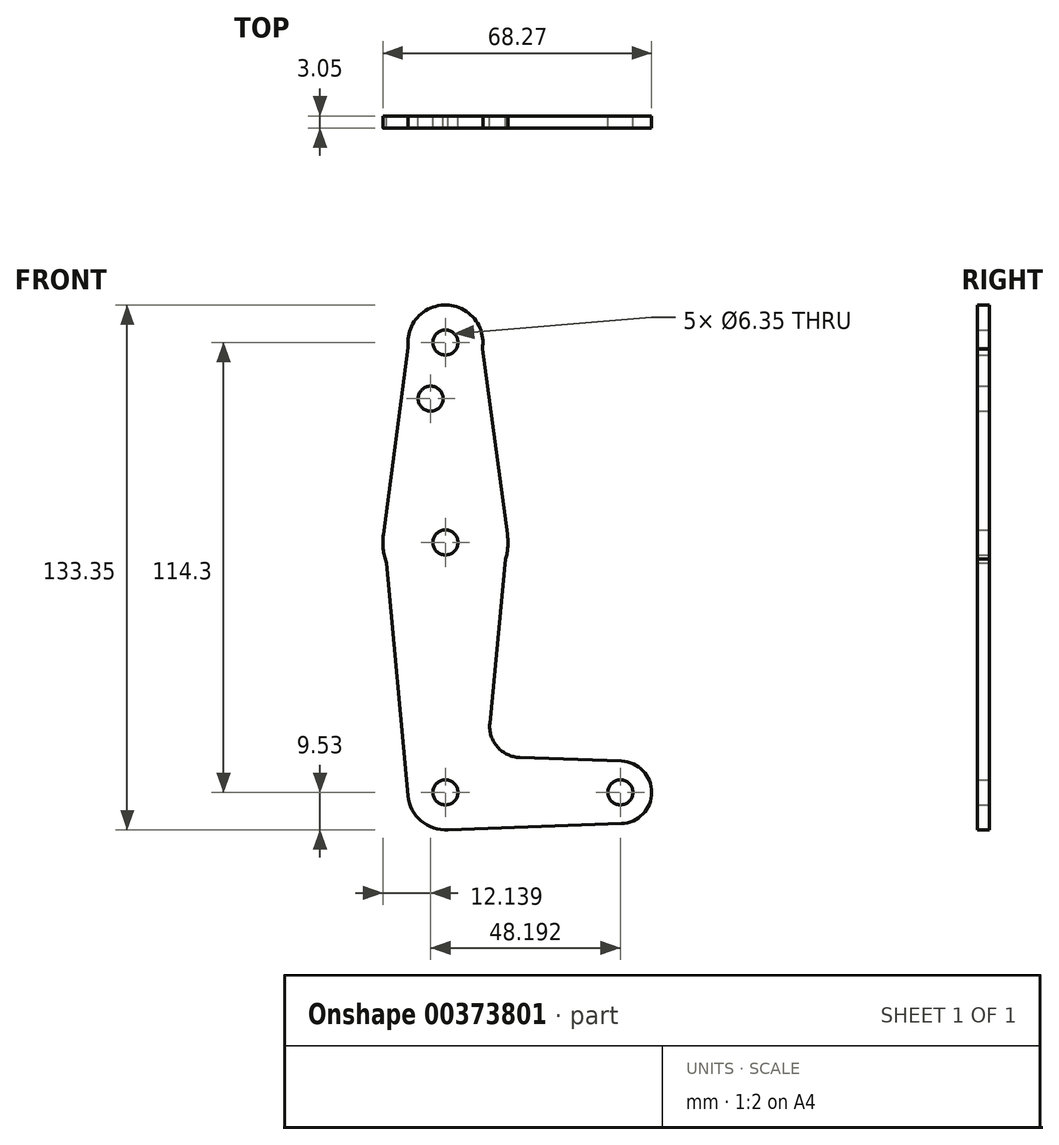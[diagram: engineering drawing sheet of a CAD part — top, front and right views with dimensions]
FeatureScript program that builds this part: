
annotation { "Feature Type Name" : "Feature", "Feature Type Description" : "" }
export const myFeature = defineFeature(function(context is Context, id is Id, definition is map)
    precondition{}
    {
        {
            var Q0;
            Q0=qCreatedBy(makeId("Front.planeOp"),FACE);
            var sketch = newSketch(context, id + "F0", { "sketchPlane" : qUnion([Q0])});
            skCircle(sketch, "E0", {"center": v(0, 0) * mm, "radius": 15.88 * mm});
            skCircle(sketch, "E1", {"center": v(0, 50.8) * mm, "radius": 9.53 * mm});
            skCircle(sketch, "E2", {"center": v(0, -63.5) * mm, "radius": 9.53 * mm});
            skLineSegment(sketch, "E3", {"start": v(0, -63.5) * mm, "end": v(44.45, -63.5) * mm, "construction": true});
            skCircle(sketch, "E4", {"center": v(44.45, -63.5) * mm, "radius": 7.94 * mm});
            skCircle(sketch, "E5", {"center": v(0, 50.8) * mm, "radius": 3.18 * mm});
            skCircle(sketch, "E6", {"center": v(0, 0) * mm, "radius": 3.18 * mm});
            skCircle(sketch, "E7", {"center": v(0, -63.5) * mm, "radius": 3.18 * mm});
            skCircle(sketch, "E8", {"center": v(44.45, -63.5) * mm, "radius": 3.18 * mm});
            skLineSegment(sketch, "E9", {"start": v(8.62, 54.85) * mm, "end": v(15.73, 2.12) * mm});
            skLineSegment(sketch, "E10", {"start": v(15.32, -4.17) * mm, "end": v(11.27, -45.94) * mm});
            skLineSegment(sketch, "E11", {"start": v(-8.8, 54.46) * mm, "end": v(-15.74, 2.09) * mm});
            skLineSegment(sketch, "E12", {"start": v(-14.99, -5.24) * mm, "end": v(-9.48, -64.38) * mm});
            skLineSegment(sketch, "E13", {"start": v(18.9, -54.65) * mm, "end": v(44.73, -55.57) * mm});
            skLineSegment(sketch, "E14", {"start": v(0, -73.02) * mm, "end": v(44.73, -71.43) * mm});
            skLineSegment(sketch, "E15", {"start": v(0, 50.8) * mm, "end": v(0, -63.5) * mm, "construction": true});
            skCircle(sketch, "E16", {"center": v(-3.74, 36.53) * mm, "radius": 3.18 * mm});
            skArc(sketch, "E17.filletArc", {"start": v(11.27, -45.94) * mm, "mid": v(13.2, -51.94) * mm, "end": v(18.9, -54.65) * mm});
            skSolve(sketch);
        }
        {
            var Q0;
            Q0 = qSketchRegion(id + "F0", true);
            extrude(context, id + "F1", {"entities" : qUnion([Q0]), "depth" : 3.05 * mm});
        }
    });
